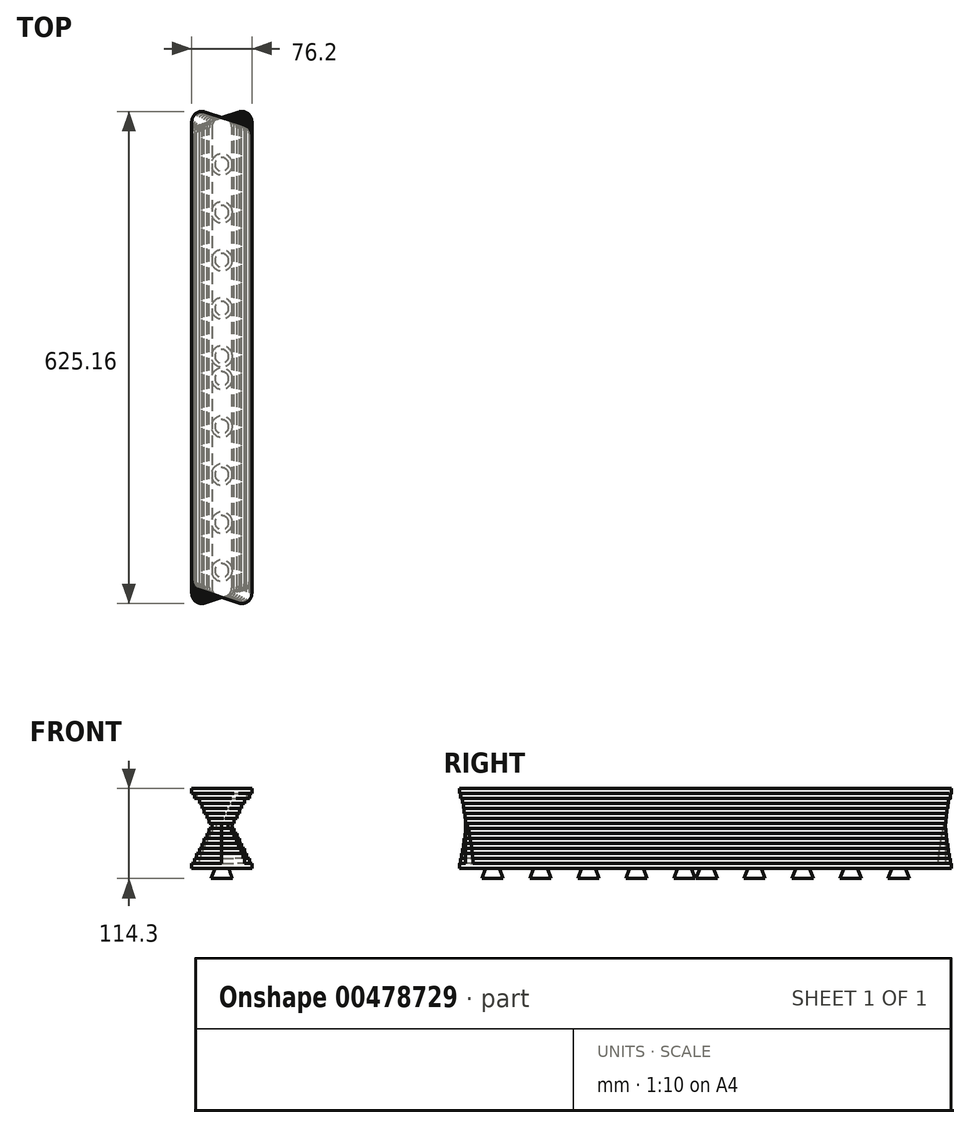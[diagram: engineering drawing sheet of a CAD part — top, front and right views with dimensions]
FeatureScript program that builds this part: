
annotation { "Feature Type Name" : "Feature", "Feature Type Description" : "" }
export const myFeature = defineFeature(function(context is Context, id is Id, definition is map)
    precondition{}
    {
        {
            var Q0;
            Q0=qCreatedBy(makeId("Top.planeOp"),FACE);
            var sketch = newSketch(context, id + "F0", { "sketchPlane" : qUnion([Q0])});
            skPoint(sketch, "E0", {"position": v(0, 0) * mm});
            skPoint(sketch, "E1", {"position": v(-38.1, 0) * mm});
            skPoint(sketch, "E2", {"position": v(-38.1, -304.8) * mm});
            skPoint(sketch, "E3", {"position": v(38.1, 0) * mm});
            skPoint(sketch, "E4", {"position": v(38.1, -279.4) * mm});
            skLineSegment(sketch, "E5", {"start": v(-38.1, 0) * mm, "end": v(-38.1, -287.18) * mm});
            skLineSegment(sketch, "E6", {"start": v(-21.38, -299.23) * mm, "end": v(29.42, -282.3) * mm});
            skLineSegment(sketch, "E7", {"start": v(38.1, -270.25) * mm, "end": v(38.1, 0) * mm});
            skArc(sketch, "E8.filletArc", {"start": v(-38.1, -287.18) * mm, "mid": v(-32.83, -297.48) * mm, "end": v(-21.38, -299.23) * mm});
            skArc(sketch, "E9.filletArc", {"start": v(29.42, -282.3) * mm, "mid": v(35.7, -277.67) * mm, "end": v(38.1, -270.25) * mm});
            skPoint(sketch, "E10", {"position": v(-38.1, 304.8) * mm});
            skPoint(sketch, "E11", {"position": v(38.1, 330.2) * mm});
            skLineSegment(sketch, "E12", {"start": v(-38.1, 0) * mm, "end": v(-38.1, 295.65) * mm});
            skLineSegment(sketch, "E13", {"start": v(-29.42, 307.7) * mm, "end": v(21.38, 324.63) * mm});
            skLineSegment(sketch, "E14", {"start": v(38.1, 312.58) * mm, "end": v(38.1, 0) * mm});
            skArc(sketch, "E15.filletArc", {"start": v(-29.42, 307.7) * mm, "mid": v(-35.7, 303.07) * mm, "end": v(-38.1, 295.65) * mm});
            skArc(sketch, "E16.filletArc", {"start": v(38.1, 312.58) * mm, "mid": v(32.83, 322.88) * mm, "end": v(21.38, 324.63) * mm});
            skSolve(sketch);
        }
        {
            var Q0;
            Q0=makeQuery(id+"F0.imprint","IMPRINT",FACE,{"disambiguationData":[TD([[makeQuery(id+"F0.imprint","IMPRINT",EDGE,{"derivedFrom":sQuery(id+"F0.wireOp",EDGE,"E5")}),1.0]])]});
            extrude(context, id + "F1", {"entities" : qUnion([Q0]), "depth" : 6.35 * mm});
        }
        {
            var Q0;
            Q0=makeQuery(id+"F1.opExtrude","CAP_FACE",FACE,{"disambiguationData":[OSD([sQuery(id+"F0.wireOp",EDGE,"E5"),sQuery(id+"F0.wireOp",EDGE,"E6"),sQuery(id+"F0.wireOp",EDGE,"E7"),sQuery(id+"F0.wireOp",EDGE,"E8.filletArc"),sQuery(id+"F0.wireOp",EDGE,"E9.filletArc"),sQuery(id+"F0.wireOp",EDGE,"E12"),sQuery(id+"F0.wireOp",EDGE,"E13"),sQuery(id+"F0.wireOp",EDGE,"E14"),sQuery(id+"F0.wireOp",EDGE,"E15.filletArc"),sQuery(id+"F0.wireOp",EDGE,"E16.filletArc")])],"isStart":false});
            var sketch = newSketch(context, id + "F2", { "sketchPlane" : qUnion([Q0])});
            skPoint(sketch, "E17", {"position": v(0, 0) * mm});
            skPoint(sketch, "E18", {"position": v(-34.93, 0) * mm});
            skPoint(sketch, "E19", {"position": v(-34.92, -303.21) * mm});
            skPoint(sketch, "E20", {"position": v(34.93, 0) * mm});
            skPoint(sketch, "E21", {"position": v(34.93, -280.99) * mm});
            skLineSegment(sketch, "E22", {"start": v(-34.93, 0) * mm, "end": v(-34.92, -285.84) * mm});
            skLineSegment(sketch, "E23", {"start": v(-18.37, -297.95) * mm, "end": v(26.08, -283.8) * mm});
            skLineSegment(sketch, "E24", {"start": v(34.93, -271.7) * mm, "end": v(34.93, 0) * mm});
            skArc(sketch, "E25.filletArc", {"start": v(-34.92, -285.84) * mm, "mid": v(-29.72, -296.1) * mm, "end": v(-18.37, -297.95) * mm});
            skArc(sketch, "E26.filletArc", {"start": v(26.08, -283.8) * mm, "mid": v(32.48, -279.2) * mm, "end": v(34.92, -271.7) * mm});
            skPoint(sketch, "E27", {"position": v(-34.93, 306.39) * mm});
            skPoint(sketch, "E28", {"position": v(34.92, 328.61) * mm});
            skLineSegment(sketch, "E29", {"start": v(-34.93, 0) * mm, "end": v(-34.93, 297.1) * mm});
            skLineSegment(sketch, "E30", {"start": v(-26.08, 309.2) * mm, "end": v(18.37, 323.35) * mm});
            skLineSegment(sketch, "E31", {"start": v(34.92, 311.24) * mm, "end": v(34.93, 0) * mm});
            skArc(sketch, "E32.filletArc", {"start": v(-26.08, 309.2) * mm, "mid": v(-32.48, 304.6) * mm, "end": v(-34.93, 297.1) * mm});
            skArc(sketch, "E33.filletArc", {"start": v(34.92, 311.24) * mm, "mid": v(29.72, 321.5) * mm, "end": v(18.37, 323.35) * mm});
            skSolve(sketch);
        }
        {
            var Q0;
            {var subQ8=sQuery(id+"F2.wireOp",EDGE,"E22");Q0=makeQuery(id+"F2.imprint","IMPRINT",FACE,{"disambiguationData":[TD([[makeQuery(id+"F2.imprint","IMPRINT",EDGE,{"derivedFrom":subQ8}),1.0]])]});}
            extrude(context, id + "F3", {"entities" : qUnion([Q0]), "depth" : 6.35 * mm});
        }
        {
            var Q0;
            Q0=makeQuery(id+"F3.opExtrude","CAP_FACE",FACE,{"disambiguationData":[OSD([sQuery(id+"F0.wireOp",EDGE,"E6"),sQuery(id+"F0.wireOp",EDGE,"E13"),sQuery(id+"F2.wireOp",EDGE,"E22"),sQuery(id+"F2.wireOp",EDGE,"E23"),sQuery(id+"F2.wireOp",EDGE,"E24"),sQuery(id+"F2.wireOp",EDGE,"E25.filletArc"),sQuery(id+"F2.wireOp",EDGE,"E26.filletArc"),sQuery(id+"F2.wireOp",EDGE,"E29"),sQuery(id+"F2.wireOp",EDGE,"E30"),sQuery(id+"F2.wireOp",EDGE,"E31"),sQuery(id+"F2.wireOp",EDGE,"E32.filletArc"),sQuery(id+"F2.wireOp",EDGE,"E33.filletArc")])],"isStart":false});
            var sketch = newSketch(context, id + "F4", { "sketchPlane" : qUnion([Q0])});
            skPoint(sketch, "E34", {"position": v(0, 0) * mm});
            skPoint(sketch, "E35", {"position": v(-31.75, 0) * mm});
            skPoint(sketch, "E36", {"position": v(-31.75, -301.63) * mm});
            skPoint(sketch, "E37", {"position": v(31.75, 0) * mm});
            skPoint(sketch, "E38", {"position": v(31.75, -282.58) * mm});
            skLineSegment(sketch, "E39", {"start": v(-31.75, 0) * mm, "end": v(-31.75, -284.56) * mm});
            skLineSegment(sketch, "E40", {"start": v(-15.4, -296.72) * mm, "end": v(22.7, -285.3) * mm});
            skLineSegment(sketch, "E41", {"start": v(31.75, -273.13) * mm, "end": v(31.75, 0) * mm});
            skArc(sketch, "E42.filletArc", {"start": v(-31.75, -284.56) * mm, "mid": v(-26.63, -294.74) * mm, "end": v(-15.4, -296.72) * mm});
            skArc(sketch, "E43.filletArc", {"start": v(22.7, -285.3) * mm, "mid": v(29.24, -280.7) * mm, "end": v(31.75, -273.13) * mm});
            skPoint(sketch, "E44.MirrorP", {"position": v(-461.86, 195.96) * mm});
            skPoint(sketch, "E45", {"position": v(-31.75, 307.98) * mm});
            skPoint(sketch, "E46", {"position": v(31.75, 327.03) * mm});
            skLineSegment(sketch, "E47", {"start": v(-31.75, 0) * mm, "end": v(-31.75, 298.53) * mm});
            skLineSegment(sketch, "E48", {"start": v(-22.7, 310.7) * mm, "end": v(15.4, 322.12) * mm});
            skLineSegment(sketch, "E49", {"start": v(31.75, 309.96) * mm, "end": v(31.75, 0) * mm});
            skArc(sketch, "E50.filletArc", {"start": v(-22.7, 310.7) * mm, "mid": v(-29.24, 306.1) * mm, "end": v(-31.75, 298.53) * mm});
            skArc(sketch, "E51.filletArc", {"start": v(31.75, 309.96) * mm, "mid": v(26.63, 320.14) * mm, "end": v(15.4, 322.12) * mm});
            skSolve(sketch);
        }
        {
            var Q0;
            {var subQ8=sQuery(id+"F4.wireOp",EDGE,"E39");Q0=makeQuery(id+"F4.imprint","IMPRINT",FACE,{"disambiguationData":[TD([[makeQuery(id+"F4.imprint","IMPRINT",EDGE,{"derivedFrom":subQ8}),1.0]])]});}
            extrude(context, id + "F5", {"entities" : qUnion([Q0]), "depth" : 6.35 * mm});
        }
        {
            var Q0;
            Q0=makeQuery(id+"F5.opExtrude","CAP_FACE",FACE,{"disambiguationData":[OSD([sQuery(id+"F0.wireOp",EDGE,"E6"),sQuery(id+"F0.wireOp",EDGE,"E13"),sQuery(id+"F4.wireOp",EDGE,"E39"),sQuery(id+"F4.wireOp",EDGE,"E40"),sQuery(id+"F4.wireOp",EDGE,"E41"),sQuery(id+"F4.wireOp",EDGE,"E42.filletArc"),sQuery(id+"F4.wireOp",EDGE,"E43.filletArc"),sQuery(id+"F4.wireOp",EDGE,"E47"),sQuery(id+"F4.wireOp",EDGE,"E48"),sQuery(id+"F4.wireOp",EDGE,"E49"),sQuery(id+"F4.wireOp",EDGE,"E50.filletArc"),sQuery(id+"F4.wireOp",EDGE,"E51.filletArc")])],"isStart":false});
            var sketch = newSketch(context, id + "F6", { "sketchPlane" : qUnion([Q0])});
            skPoint(sketch, "E52", {"position": v(0, 0) * mm});
            skPoint(sketch, "E53", {"position": v(-28.58, 0) * mm});
            skPoint(sketch, "E54", {"position": v(-28.57, -300.04) * mm});
            skPoint(sketch, "E55", {"position": v(28.58, 0) * mm});
            skPoint(sketch, "E56", {"position": v(28.58, -284.16) * mm});
            skLineSegment(sketch, "E57", {"start": v(-28.58, 0) * mm, "end": v(-28.57, -283.33) * mm});
            skLineSegment(sketch, "E58", {"start": v(-12.48, -295.57) * mm, "end": v(19.27, -286.75) * mm});
            skLineSegment(sketch, "E59", {"start": v(28.58, -274.5) * mm, "end": v(28.58, 0) * mm});
            skArc(sketch, "E60.filletArc", {"start": v(-28.57, -283.33) * mm, "mid": v(-23.56, -293.44) * mm, "end": v(-12.48, -295.57) * mm});
            skArc(sketch, "E61.filletArc", {"start": v(19.27, -286.75) * mm, "mid": v(25.99, -282.2) * mm, "end": v(28.57, -274.5) * mm});
            skPoint(sketch, "E62.MirrorP", {"position": v(-895.77, 331.85) * mm});
            skPoint(sketch, "E63", {"position": v(-28.58, 309.56) * mm});
            skPoint(sketch, "E64", {"position": v(28.57, 325.44) * mm});
            skLineSegment(sketch, "E65", {"start": v(-28.58, 0) * mm, "end": v(-28.58, 299.9) * mm});
            skLineSegment(sketch, "E66", {"start": v(-19.27, 312.15) * mm, "end": v(12.48, 320.97) * mm});
            skLineSegment(sketch, "E67", {"start": v(28.57, 308.73) * mm, "end": v(28.58, 0) * mm});
            skArc(sketch, "E68.filletArc", {"start": v(-19.27, 312.15) * mm, "mid": v(-25.99, 307.6) * mm, "end": v(-28.58, 299.9) * mm});
            skArc(sketch, "E69.filletArc", {"start": v(28.57, 308.73) * mm, "mid": v(23.56, 318.84) * mm, "end": v(12.48, 320.97) * mm});
            skSolve(sketch);
        }
        {
            var Q0;
            Q0=makeQuery(id+"F6.imprint","IMPRINT",FACE,{"disambiguationData":[TD([[makeQuery(id+"F6.imprint","IMPRINT",EDGE,{"derivedFrom":sQuery(id+"F6.wireOp",EDGE,"E57")}),1.0]])]});
            extrude(context, id + "F7", {"entities" : qUnion([Q0]), "depth" : 6.35 * mm});
        }
        {
            var Q0;
            Q0=makeQuery(id+"F7.opExtrude","CAP_FACE",FACE,{"disambiguationData":[OSD([sQuery(id+"F0.wireOp",EDGE,"E6"),sQuery(id+"F0.wireOp",EDGE,"E13"),sQuery(id+"F6.wireOp",EDGE,"E57"),sQuery(id+"F6.wireOp",EDGE,"E58"),sQuery(id+"F6.wireOp",EDGE,"E59"),sQuery(id+"F6.wireOp",EDGE,"E60.filletArc"),sQuery(id+"F6.wireOp",EDGE,"E61.filletArc"),sQuery(id+"F6.wireOp",EDGE,"E65"),sQuery(id+"F6.wireOp",EDGE,"E66"),sQuery(id+"F6.wireOp",EDGE,"E67"),sQuery(id+"F6.wireOp",EDGE,"E68.filletArc"),sQuery(id+"F6.wireOp",EDGE,"E69.filletArc")])],"isStart":false});
            var sketch = newSketch(context, id + "F8", { "sketchPlane" : qUnion([Q0])});
            skPoint(sketch, "E70", {"position": v(0, 0) * mm});
            skPoint(sketch, "E71", {"position": v(-25.4, 0) * mm});
            skPoint(sketch, "E72", {"position": v(-25.4, -298.45) * mm});
            skPoint(sketch, "E73", {"position": v(25.4, 0) * mm});
            skPoint(sketch, "E74", {"position": v(25.4, -285.75) * mm});
            skLineSegment(sketch, "E75", {"start": v(-25.4, 0) * mm, "end": v(-25.4, -282.18) * mm});
            skLineSegment(sketch, "E76", {"start": v(-9.62, -294.5) * mm, "end": v(15.78, -288.15) * mm});
            skLineSegment(sketch, "E77", {"start": v(25.4, -275.83) * mm, "end": v(25.4, 0) * mm});
            skArc(sketch, "E78.filletArc", {"start": v(-25.4, -282.18) * mm, "mid": v(-20.52, -292.2) * mm, "end": v(-9.62, -294.5) * mm});
            skArc(sketch, "E79.filletArc", {"start": v(15.78, -288.15) * mm, "mid": v(22.71, -283.65) * mm, "end": v(25.4, -275.83) * mm});
            skPoint(sketch, "E80.MirrorP", {"position": v(-1189.04, 488.26) * mm});
            skPoint(sketch, "E81", {"position": v(-25.4, 311.15) * mm});
            skPoint(sketch, "E82", {"position": v(25.4, 323.85) * mm});
            skLineSegment(sketch, "E83", {"start": v(-25.4, 0) * mm, "end": v(-25.4, 301.23) * mm});
            skLineSegment(sketch, "E84", {"start": v(-15.78, 313.55) * mm, "end": v(9.62, 319.9) * mm});
            skLineSegment(sketch, "E85", {"start": v(25.4, 307.58) * mm, "end": v(25.4, 0) * mm});
            skArc(sketch, "E86.filletArc", {"start": v(-15.78, 313.55) * mm, "mid": v(-22.71, 309.05) * mm, "end": v(-25.4, 301.23) * mm});
            skArc(sketch, "E87.filletArc", {"start": v(25.4, 307.58) * mm, "mid": v(20.52, 317.6) * mm, "end": v(9.62, 319.9) * mm});
            skSolve(sketch);
        }
        {
            var Q0;
            Q0=makeQuery(id+"F8.imprint","IMPRINT",FACE,{"disambiguationData":[TD([[makeQuery(id+"F8.imprint","IMPRINT",EDGE,{"derivedFrom":sQuery(id+"F8.wireOp",EDGE,"E75")}),1.0]])]});
            extrude(context, id + "F9", {"entities" : qUnion([Q0]), "depth" : 6.35 * mm});
        }
        {
            var Q0;
            Q0=makeQuery(id+"F9.opExtrude","CAP_FACE",FACE,{"disambiguationData":[OSD([sQuery(id+"F0.wireOp",EDGE,"E6"),sQuery(id+"F0.wireOp",EDGE,"E13"),sQuery(id+"F8.wireOp",EDGE,"E75"),sQuery(id+"F8.wireOp",EDGE,"E76"),sQuery(id+"F8.wireOp",EDGE,"E77"),sQuery(id+"F8.wireOp",EDGE,"E78.filletArc"),sQuery(id+"F8.wireOp",EDGE,"E79.filletArc"),sQuery(id+"F8.wireOp",EDGE,"E83"),sQuery(id+"F8.wireOp",EDGE,"E84"),sQuery(id+"F8.wireOp",EDGE,"E85"),sQuery(id+"F8.wireOp",EDGE,"E86.filletArc"),sQuery(id+"F8.wireOp",EDGE,"E87.filletArc")])],"isStart":false});
            var sketch = newSketch(context, id + "F10", { "sketchPlane" : qUnion([Q0])});
            skPoint(sketch, "E88", {"position": v(0, 0) * mm});
            skPoint(sketch, "E89", {"position": v(-22.23, 0) * mm});
            skPoint(sketch, "E90", {"position": v(-22.22, -296.86) * mm});
            skPoint(sketch, "E91", {"position": v(22.23, 0) * mm});
            skPoint(sketch, "E92", {"position": v(22.23, -287.34) * mm});
            skLineSegment(sketch, "E93", {"start": v(-22.23, 0) * mm, "end": v(-22.22, -281.15) * mm});
            skLineSegment(sketch, "E94", {"start": v(-6.86, -293.57) * mm, "end": v(12.19, -289.49) * mm});
            skLineSegment(sketch, "E95", {"start": v(22.23, -277.07) * mm, "end": v(22.23, 0) * mm});
            skArc(sketch, "E96.filletArc", {"start": v(-22.22, -281.15) * mm, "mid": v(-17.5, -291.03) * mm, "end": v(-6.86, -293.57) * mm});
            skArc(sketch, "E97.filletArc", {"start": v(12.19, -289.49) * mm, "mid": v(19.4, -285.05) * mm, "end": v(22.22, -277.07) * mm});
            skPoint(sketch, "E98.MirrorP", {"position": v(-1110.6, 407.11) * mm});
            skPoint(sketch, "E99", {"position": v(-22.23, 312.74) * mm});
            skPoint(sketch, "E100", {"position": v(22.22, 322.26) * mm});
            skLineSegment(sketch, "E101", {"start": v(-22.23, 0) * mm, "end": v(-22.23, 302.47) * mm});
            skLineSegment(sketch, "E102", {"start": v(-12.19, 314.89) * mm, "end": v(6.86, 318.97) * mm});
            skLineSegment(sketch, "E103", {"start": v(22.22, 306.55) * mm, "end": v(22.23, 0) * mm});
            skArc(sketch, "E104.filletArc", {"start": v(-12.19, 314.89) * mm, "mid": v(-19.4, 310.45) * mm, "end": v(-22.23, 302.47) * mm});
            skArc(sketch, "E105.filletArc", {"start": v(22.22, 306.55) * mm, "mid": v(17.5, 316.43) * mm, "end": v(6.86, 318.97) * mm});
            skSolve(sketch);
        }
        {
            var Q0;
            Q0=makeQuery(id+"F10.imprint","IMPRINT",FACE,{"disambiguationData":[TD([[makeQuery(id+"F10.imprint","IMPRINT",EDGE,{"derivedFrom":sQuery(id+"F10.wireOp",EDGE,"E93")}),1.0]])]});
            extrude(context, id + "F11", {"entities" : qUnion([Q0]), "depth" : 6.35 * mm});
        }
        {
            var Q0;
            Q0=makeQuery(id+"F11.opExtrude","CAP_FACE",FACE,{"disambiguationData":[OSD([sQuery(id+"F0.wireOp",EDGE,"E6"),sQuery(id+"F0.wireOp",EDGE,"E13"),sQuery(id+"F10.wireOp",EDGE,"E93"),sQuery(id+"F10.wireOp",EDGE,"E94"),sQuery(id+"F10.wireOp",EDGE,"E95"),sQuery(id+"F10.wireOp",EDGE,"E96.filletArc"),sQuery(id+"F10.wireOp",EDGE,"E97.filletArc"),sQuery(id+"F10.wireOp",EDGE,"E101"),sQuery(id+"F10.wireOp",EDGE,"E102"),sQuery(id+"F10.wireOp",EDGE,"E103"),sQuery(id+"F10.wireOp",EDGE,"E104.filletArc"),sQuery(id+"F10.wireOp",EDGE,"E105.filletArc")])],"isStart":false});
            var sketch = newSketch(context, id + "F12", { "sketchPlane" : qUnion([Q0])});
            skPoint(sketch, "E106", {"position": v(0, 0) * mm});
            skPoint(sketch, "E107", {"position": v(-19.05, 0) * mm});
            skPoint(sketch, "E108", {"position": v(-19.05, -295.28) * mm});
            skPoint(sketch, "E109", {"position": v(19.05, 0) * mm});
            skPoint(sketch, "E110", {"position": v(19.05, -288.93) * mm});
            skLineSegment(sketch, "E111", {"start": v(-19.05, 0) * mm, "end": v(-19.05, -280.28) * mm});
            skLineSegment(sketch, "E112", {"start": v(-4.26, -292.81) * mm, "end": v(8.44, -290.7) * mm});
            skLineSegment(sketch, "E113", {"start": v(19.05, -278.17) * mm, "end": v(19.05, 0) * mm});
            skArc(sketch, "E114.filletArc", {"start": v(-19.05, -280.28) * mm, "mid": v(-14.56, -289.97) * mm, "end": v(-4.26, -292.81) * mm});
            skArc(sketch, "E115.filletArc", {"start": v(8.44, -290.7) * mm, "mid": v(16.04, -286.38) * mm, "end": v(19.05, -278.17) * mm});
            skPoint(sketch, "E116.MirrorP", {"position": v(-1134.4, 517.38) * mm});
            skPoint(sketch, "E117", {"position": v(-19.05, 314.33) * mm});
            skPoint(sketch, "E118", {"position": v(19.05, 320.68) * mm});
            skLineSegment(sketch, "E119", {"start": v(-19.05, 0) * mm, "end": v(-19.05, 303.57) * mm});
            skLineSegment(sketch, "E120", {"start": v(-8.44, 316.1) * mm, "end": v(4.26, 318.21) * mm});
            skLineSegment(sketch, "E121", {"start": v(19.05, 305.68) * mm, "end": v(19.05, 0) * mm});
            skArc(sketch, "E122.filletArc", {"start": v(-8.44, 316.1) * mm, "mid": v(-16.04, 311.78) * mm, "end": v(-19.05, 303.57) * mm});
            skArc(sketch, "E123.filletArc", {"start": v(19.05, 305.68) * mm, "mid": v(14.56, 315.37) * mm, "end": v(4.26, 318.21) * mm});
            skSolve(sketch);
        }
        {
            var Q0;
            {var subQ12=sQuery(id+"F12.wireOp",EDGE,"E113");Q0=makeQuery(id+"F12.imprint","IMPRINT",FACE,{"disambiguationData":[TD([[makeQuery(id+"F12.imprint","IMPRINT",EDGE,{"derivedFrom":subQ12}),1.0]])]});}
            extrude(context, id + "F13", {"entities" : qUnion([Q0]), "depth" : 6.35 * mm});
        }
        {
            var Q0;
            Q0=makeQuery(id+"F13.opExtrude","CAP_FACE",FACE,{"disambiguationData":[OSD([sQuery(id+"F0.wireOp",EDGE,"E6"),sQuery(id+"F0.wireOp",EDGE,"E13"),sQuery(id+"F10.wireOp",EDGE,"E93"),sQuery(id+"F10.wireOp",EDGE,"E96.filletArc"),sQuery(id+"F10.wireOp",EDGE,"E101"),sQuery(id+"F10.wireOp",EDGE,"E102"),sQuery(id+"F10.wireOp",EDGE,"E104.filletArc"),sQuery(id+"F12.wireOp",EDGE,"E112"),sQuery(id+"F12.wireOp",EDGE,"E113"),sQuery(id+"F12.wireOp",EDGE,"E115.filletArc"),sQuery(id+"F12.wireOp",EDGE,"E121"),sQuery(id+"F12.wireOp",EDGE,"E123.filletArc")])],"isStart":false});
            var sketch = newSketch(context, id + "F14", { "sketchPlane" : qUnion([Q0])});
            skPoint(sketch, "E124", {"position": v(0, 0) * mm});
            skPoint(sketch, "E125", {"position": v(-15.88, 0) * mm});
            skPoint(sketch, "E126", {"position": v(-15.87, -293.69) * mm});
            skPoint(sketch, "E127", {"position": v(15.88, 0) * mm});
            skPoint(sketch, "E128", {"position": v(15.88, -290.51) * mm});
            skLineSegment(sketch, "E129", {"start": v(-15.88, 0) * mm, "end": v(-15.87, -279.65) * mm});
            skLineSegment(sketch, "E130", {"start": v(-1.91, -292.3) * mm, "end": v(4.44, -291.66) * mm});
            skLineSegment(sketch, "E131", {"start": v(15.88, -279.02) * mm, "end": v(15.88, 0) * mm});
            skArc(sketch, "E132.filletArc", {"start": v(-15.87, -279.65) * mm, "mid": v(-11.7, -289.07) * mm, "end": v(-1.91, -292.3) * mm});
            skArc(sketch, "E133.filletArc", {"start": v(4.44, -291.66) * mm, "mid": v(12.6, -287.54) * mm, "end": v(15.88, -279.02) * mm});
            skPoint(sketch, "E134.MirrorP", {"position": v(-1354.1, 474.43) * mm});
            skPoint(sketch, "E135", {"position": v(-15.88, 315.91) * mm});
            skPoint(sketch, "E136", {"position": v(15.87, 319.09) * mm});
            skLineSegment(sketch, "E137", {"start": v(-15.88, 0) * mm, "end": v(-15.88, 304.42) * mm});
            skLineSegment(sketch, "E138", {"start": v(-4.44, 317.06) * mm, "end": v(1.91, 317.7) * mm});
            skLineSegment(sketch, "E139", {"start": v(15.87, 305.05) * mm, "end": v(15.88, 0) * mm});
            skArc(sketch, "E140.filletArc", {"start": v(-4.44, 317.06) * mm, "mid": v(-12.6, 312.94) * mm, "end": v(-15.88, 304.42) * mm});
            skArc(sketch, "E141.filletArc", {"start": v(15.87, 305.05) * mm, "mid": v(11.7, 314.47) * mm, "end": v(1.91, 317.7) * mm});
            skSolve(sketch);
        }
        {
            var Q0;
            Q0=makeQuery(id+"F14.imprint","IMPRINT",FACE,{"disambiguationData":[TD([[makeQuery(id+"F14.imprint","IMPRINT",EDGE,{"derivedFrom":sQuery(id+"F14.wireOp",EDGE,"E129")}),1.0]])]});
            extrude(context, id + "F15", {"entities" : qUnion([Q0]), "depth" : 6.35 * mm});
        }
        {
            var Q0;
            Q0=makeQuery(id+"F15.opExtrude","CAP_FACE",FACE,{"disambiguationData":[OSD([sQuery(id+"F0.wireOp",EDGE,"E6"),sQuery(id+"F0.wireOp",EDGE,"E13"),sQuery(id+"F14.wireOp",EDGE,"E129"),sQuery(id+"F14.wireOp",EDGE,"E130"),sQuery(id+"F14.wireOp",EDGE,"E131"),sQuery(id+"F14.wireOp",EDGE,"E132.filletArc"),sQuery(id+"F14.wireOp",EDGE,"E133.filletArc"),sQuery(id+"F14.wireOp",EDGE,"E137"),sQuery(id+"F14.wireOp",EDGE,"E138"),sQuery(id+"F14.wireOp",EDGE,"E139"),sQuery(id+"F14.wireOp",EDGE,"E140.filletArc"),sQuery(id+"F14.wireOp",EDGE,"E141.filletArc")])],"isStart":false});
            var sketch = newSketch(context, id + "F16", { "sketchPlane" : qUnion([Q0])});
            skPoint(sketch, "E142", {"position": v(0, 0) * mm});
            skPoint(sketch, "E143", {"position": v(-12.7, 0) * mm});
            skPoint(sketch, "E144", {"position": v(-12.7, -292.1) * mm});
            skPoint(sketch, "E145", {"position": v(12.7, 0) * mm});
            skPoint(sketch, "E146", {"position": v(12.7, -292.1) * mm});
            skLineSegment(sketch, "E147", {"start": v(-12.7, 0) * mm, "end": v(-12.7, -279.4) * mm});
            skLineSegment(sketch, "E148", {"start": v(0, -292.1) * mm, "end": v(0, -292.1) * mm});
            skLineSegment(sketch, "E149", {"start": v(12.7, -279.4) * mm, "end": v(12.7, 0) * mm});
            skArc(sketch, "E150.filletArc", {"start": v(-12.7, -279.4) * mm, "mid": v(-8.98, -288.38) * mm, "end": v(0, -292.1) * mm});
            skArc(sketch, "E151.filletArc", {"start": v(0, -292.1) * mm, "mid": v(8.98, -288.38) * mm, "end": v(12.7, -279.4) * mm});
            skPoint(sketch, "E152.MirrorP", {"position": v(-1174.77, 259.43) * mm});
            skPoint(sketch, "E153", {"position": v(-12.7, 317.5) * mm});
            skPoint(sketch, "E154", {"position": v(12.7, 317.5) * mm});
            skLineSegment(sketch, "E155", {"start": v(-12.7, 0) * mm, "end": v(-12.7, 304.8) * mm});
            skLineSegment(sketch, "E156", {"start": v(0, 317.5) * mm, "end": v(0, 317.5) * mm});
            skLineSegment(sketch, "E157", {"start": v(12.7, 304.8) * mm, "end": v(12.7, 0) * mm});
            skArc(sketch, "E158.filletArc", {"start": v(0, 317.5) * mm, "mid": v(-8.98, 313.78) * mm, "end": v(-12.7, 304.8) * mm});
            skArc(sketch, "E159.filletArc", {"start": v(12.7, 304.8) * mm, "mid": v(8.98, 313.78) * mm, "end": v(0, 317.5) * mm});
            skSolve(sketch);
        }
        {
            var Q0;
            Q0=makeQuery(id+"F16.imprint","IMPRINT",FACE,{"disambiguationData":[TD([[makeQuery(id+"F16.imprint","IMPRINT",EDGE,{"derivedFrom":sQuery(id+"F16.wireOp",EDGE,"E147")}),1.0]])]});
            extrude(context, id + "F17", {"entities" : qUnion([Q0]), "depth" : 6.35 * mm});
        }
        {
            var Q0;
            Q0=makeQuery(id+"F17.opExtrude","CAP_FACE",FACE,{"disambiguationData":[OSD([sQuery(id+"F0.wireOp",EDGE,"E6"),sQuery(id+"F0.wireOp",EDGE,"E13"),sQuery(id+"F16.wireOp",EDGE,"E147"),sQuery(id+"F16.wireOp",EDGE,"E149"),sQuery(id+"F16.wireOp",EDGE,"E150.filletArc"),sQuery(id+"F16.wireOp",EDGE,"E151.filletArc"),sQuery(id+"F16.wireOp",EDGE,"E155"),sQuery(id+"F16.wireOp",EDGE,"E157"),sQuery(id+"F16.wireOp",EDGE,"E158.filletArc"),sQuery(id+"F16.wireOp",EDGE,"E159.filletArc")])],"isStart":false});
            var sketch = newSketch(context, id + "F18", { "sketchPlane" : qUnion([Q0])});
            skPoint(sketch, "E160", {"position": v(0, 0) * mm});
            skPoint(sketch, "E161", {"position": v(-15.88, 0) * mm});
            skPoint(sketch, "E162", {"position": v(-15.87, -290.51) * mm});
            skPoint(sketch, "E163", {"position": v(15.88, 0) * mm});
            skPoint(sketch, "E164", {"position": v(15.88, -293.69) * mm});
            skLineSegment(sketch, "E165", {"start": v(-15.88, 0) * mm, "end": v(-15.87, -279.02) * mm});
            skLineSegment(sketch, "E166", {"start": v(-4.44, -291.66) * mm, "end": v(1.91, -292.3) * mm});
            skLineSegment(sketch, "E167", {"start": v(15.88, -279.65) * mm, "end": v(15.88, 0) * mm});
            skArc(sketch, "E168.filletArc", {"start": v(-15.87, -279.02) * mm, "mid": v(-12.6, -287.54) * mm, "end": v(-4.44, -291.66) * mm});
            skArc(sketch, "E169.filletArc", {"start": v(1.91, -292.3) * mm, "mid": v(11.7, -289.07) * mm, "end": v(15.87, -279.65) * mm});
            skPoint(sketch, "E170.MirrorP", {"position": v(-1386.88, 490.35) * mm});
            skPoint(sketch, "E171", {"position": v(-15.88, 319.09) * mm});
            skPoint(sketch, "E172", {"position": v(15.87, 315.91) * mm});
            skLineSegment(sketch, "E173", {"start": v(-15.88, 0) * mm, "end": v(-15.88, 305.05) * mm});
            skLineSegment(sketch, "E174", {"start": v(-1.91, 317.7) * mm, "end": v(4.44, 317.06) * mm});
            skLineSegment(sketch, "E175", {"start": v(15.87, 304.42) * mm, "end": v(15.88, 0) * mm});
            skArc(sketch, "E176.filletArc", {"start": v(-1.91, 317.7) * mm, "mid": v(-11.7, 314.47) * mm, "end": v(-15.88, 305.05) * mm});
            skArc(sketch, "E177.filletArc", {"start": v(15.87, 304.42) * mm, "mid": v(12.6, 312.94) * mm, "end": v(4.44, 317.06) * mm});
            skSolve(sketch);
        }
        {
            var Q0;
            Q0=qSketchRegion(id+"F18",true);
            extrude(context, id + "F19", {"entities" : qUnion([Q0]), "depth" : 6.35 * mm});
        }
        {
            var Q0;
            Q0=makeQuery(id+"F19.opExtrude","CAP_FACE",FACE,{"disambiguationData":[OSD([sQuery(id+"F0.wireOp",EDGE,"E6"),sQuery(id+"F0.wireOp",EDGE,"E13"),sQuery(id+"F16.wireOp",EDGE,"E147"),sQuery(id+"F16.wireOp",EDGE,"E149"),sQuery(id+"F16.wireOp",EDGE,"E150.filletArc"),sQuery(id+"F16.wireOp",EDGE,"E151.filletArc"),sQuery(id+"F16.wireOp",EDGE,"E155"),sQuery(id+"F16.wireOp",EDGE,"E157"),sQuery(id+"F16.wireOp",EDGE,"E158.filletArc"),sQuery(id+"F16.wireOp",EDGE,"E159.filletArc"),sQuery(id+"F18.wireOp",EDGE,"E166"),sQuery(id+"F18.wireOp",EDGE,"E174")])],"isStart":false});
            var sketch = newSketch(context, id + "F20", { "sketchPlane" : qUnion([Q0])});
            skPoint(sketch, "E178", {"position": v(0, 0) * mm});
            skPoint(sketch, "E179", {"position": v(-19.05, 0) * mm});
            skPoint(sketch, "E180", {"position": v(-19.05, -288.93) * mm});
            skPoint(sketch, "E181", {"position": v(19.05, 0) * mm});
            skPoint(sketch, "E182", {"position": v(19.05, -295.28) * mm});
            skLineSegment(sketch, "E183", {"start": v(-19.05, 0) * mm, "end": v(-19.05, -278.17) * mm});
            skLineSegment(sketch, "E184", {"start": v(-8.44, -290.7) * mm, "end": v(4.26, -292.81) * mm});
            skLineSegment(sketch, "E185", {"start": v(19.05, -280.28) * mm, "end": v(19.05, 0) * mm});
            skArc(sketch, "E186.filletArc", {"start": v(-19.05, -278.17) * mm, "mid": v(-16.04, -286.38) * mm, "end": v(-8.44, -290.7) * mm});
            skArc(sketch, "E187.filletArc", {"start": v(4.26, -292.81) * mm, "mid": v(14.56, -289.97) * mm, "end": v(19.05, -280.28) * mm});
            skPoint(sketch, "E188.MirrorP", {"position": v(-2251.33, 639) * mm});
            skPoint(sketch, "E189", {"position": v(-19.05, 320.68) * mm});
            skPoint(sketch, "E190", {"position": v(19.05, 314.33) * mm});
            skLineSegment(sketch, "E191", {"start": v(-19.05, 0) * mm, "end": v(-19.05, 305.68) * mm});
            skLineSegment(sketch, "E192", {"start": v(-4.26, 318.21) * mm, "end": v(8.44, 316.1) * mm});
            skLineSegment(sketch, "E193", {"start": v(19.05, 303.57) * mm, "end": v(19.05, 0) * mm});
            skArc(sketch, "E194.filletArc", {"start": v(-4.26, 318.21) * mm, "mid": v(-14.56, 315.37) * mm, "end": v(-19.05, 305.68) * mm});
            skArc(sketch, "E195.filletArc", {"start": v(19.05, 303.57) * mm, "mid": v(16.04, 311.78) * mm, "end": v(8.44, 316.1) * mm});
            skSolve(sketch);
        }
        {
            var Q0;
            Q0=qSketchRegion(id+"F20",true);
            extrude(context, id + "F21", {"entities" : qUnion([Q0]), "depth" : 6.35 * mm});
        }
        {
            var Q0;
            Q0=makeQuery(id+"F21.opExtrude","CAP_FACE",FACE,{"disambiguationData":[OSD([sQuery(id+"F0.wireOp",EDGE,"E6"),sQuery(id+"F0.wireOp",EDGE,"E13"),sQuery(id+"F16.wireOp",EDGE,"E147"),sQuery(id+"F16.wireOp",EDGE,"E149"),sQuery(id+"F16.wireOp",EDGE,"E150.filletArc"),sQuery(id+"F16.wireOp",EDGE,"E151.filletArc"),sQuery(id+"F16.wireOp",EDGE,"E155"),sQuery(id+"F16.wireOp",EDGE,"E157"),sQuery(id+"F16.wireOp",EDGE,"E158.filletArc"),sQuery(id+"F16.wireOp",EDGE,"E159.filletArc"),sQuery(id+"F20.wireOp",EDGE,"E184"),sQuery(id+"F20.wireOp",EDGE,"E192")])],"isStart":false});
            var sketch = newSketch(context, id + "F22", { "sketchPlane" : qUnion([Q0])});
            skPoint(sketch, "E196", {"position": v(0, 0) * mm});
            skPoint(sketch, "E197", {"position": v(-22.23, 0) * mm});
            skPoint(sketch, "E198", {"position": v(-22.22, -287.34) * mm});
            skPoint(sketch, "E199", {"position": v(22.23, 0) * mm});
            skPoint(sketch, "E200", {"position": v(22.23, -296.86) * mm});
            skLineSegment(sketch, "E201", {"start": v(-22.23, 0) * mm, "end": v(-22.22, -277.07) * mm});
            skLineSegment(sketch, "E202", {"start": v(-12.19, -289.49) * mm, "end": v(6.86, -293.57) * mm});
            skLineSegment(sketch, "E203", {"start": v(22.23, -281.15) * mm, "end": v(22.23, 0) * mm});
            skArc(sketch, "E204.filletArc", {"start": v(-22.22, -277.07) * mm, "mid": v(-19.4, -285.05) * mm, "end": v(-12.19, -289.49) * mm});
            skArc(sketch, "E205.filletArc", {"start": v(6.86, -293.57) * mm, "mid": v(17.5, -291.03) * mm, "end": v(22.22, -281.15) * mm});
            skPoint(sketch, "E206.MirrorP", {"position": v(-2054.65, 833.78) * mm});
            skPoint(sketch, "E207", {"position": v(-22.23, 322.26) * mm});
            skPoint(sketch, "E208", {"position": v(22.22, 312.74) * mm});
            skLineSegment(sketch, "E209", {"start": v(-22.23, 0) * mm, "end": v(-22.23, 306.55) * mm});
            skLineSegment(sketch, "E210", {"start": v(-6.86, 318.97) * mm, "end": v(12.19, 314.89) * mm});
            skLineSegment(sketch, "E211", {"start": v(22.22, 302.47) * mm, "end": v(22.23, 0) * mm});
            skArc(sketch, "E212.filletArc", {"start": v(-6.86, 318.97) * mm, "mid": v(-17.5, 316.43) * mm, "end": v(-22.23, 306.55) * mm});
            skArc(sketch, "E213.filletArc", {"start": v(22.22, 302.47) * mm, "mid": v(19.4, 310.45) * mm, "end": v(12.19, 314.89) * mm});
            skSolve(sketch);
        }
        {
            var Q0;
            Q0=qSketchRegion(id+"F22",true);
            extrude(context, id + "F23", {"entities" : qUnion([Q0]), "depth" : 6.35 * mm});
        }
        {
            var Q0;
            Q0=makeQuery(id+"F23.opExtrude","CAP_FACE",FACE,{"disambiguationData":[OSD([sQuery(id+"F22.wireOp",EDGE,"E201"),sQuery(id+"F22.wireOp",EDGE,"E202"),sQuery(id+"F22.wireOp",EDGE,"E203"),sQuery(id+"F22.wireOp",EDGE,"E204.filletArc"),sQuery(id+"F22.wireOp",EDGE,"E205.filletArc"),sQuery(id+"F22.wireOp",EDGE,"E209"),sQuery(id+"F22.wireOp",EDGE,"E210"),sQuery(id+"F22.wireOp",EDGE,"E211"),sQuery(id+"F22.wireOp",EDGE,"E212.filletArc"),sQuery(id+"F22.wireOp",EDGE,"E213.filletArc")])],"isStart":false});
            var sketch = newSketch(context, id + "F24", { "sketchPlane" : qUnion([Q0])});
            skPoint(sketch, "E214", {"position": v(0, 0) * mm});
            skPoint(sketch, "E215", {"position": v(-25.4, 0) * mm});
            skPoint(sketch, "E216", {"position": v(-25.4, -285.75) * mm});
            skPoint(sketch, "E217", {"position": v(25.4, 0) * mm});
            skPoint(sketch, "E218", {"position": v(25.4, -298.45) * mm});
            skLineSegment(sketch, "E219", {"start": v(-25.4, 0) * mm, "end": v(-25.4, -275.83) * mm});
            skLineSegment(sketch, "E220", {"start": v(-15.78, -288.15) * mm, "end": v(9.62, -294.5) * mm});
            skLineSegment(sketch, "E221", {"start": v(25.4, -282.18) * mm, "end": v(25.4, 0) * mm});
            skArc(sketch, "E222.filletArc", {"start": v(-25.4, -275.83) * mm, "mid": v(-22.71, -283.65) * mm, "end": v(-15.78, -288.15) * mm});
            skArc(sketch, "E223.filletArc", {"start": v(9.62, -294.5) * mm, "mid": v(20.52, -292.2) * mm, "end": v(25.4, -282.18) * mm});
            skPoint(sketch, "E224.MirrorP", {"position": v(-1763.83, 631.7) * mm});
            skPoint(sketch, "E225", {"position": v(-25.4, 323.85) * mm});
            skPoint(sketch, "E226", {"position": v(25.4, 311.15) * mm});
            skLineSegment(sketch, "E227", {"start": v(-25.4, 0) * mm, "end": v(-25.4, 307.58) * mm});
            skLineSegment(sketch, "E228", {"start": v(-9.62, 319.9) * mm, "end": v(15.78, 313.55) * mm});
            skLineSegment(sketch, "E229", {"start": v(25.4, 301.23) * mm, "end": v(25.4, 0) * mm});
            skArc(sketch, "E230.filletArc", {"start": v(-9.62, 319.9) * mm, "mid": v(-20.52, 317.6) * mm, "end": v(-25.4, 307.58) * mm});
            skArc(sketch, "E231.filletArc", {"start": v(25.4, 301.23) * mm, "mid": v(22.71, 309.05) * mm, "end": v(15.78, 313.55) * mm});
            skSolve(sketch);
        }
        {
            var Q0;
            Q0=qSketchRegion(id+"F24",true);
            extrude(context, id + "F25", {"entities" : qUnion([Q0]), "depth" : 6.35 * mm});
        }
        {
            var Q0;
            Q0=makeQuery(id+"F25.opExtrude","CAP_FACE",FACE,{"disambiguationData":[OSD([sQuery(id+"F24.wireOp",EDGE,"E219"),sQuery(id+"F24.wireOp",EDGE,"E220"),sQuery(id+"F24.wireOp",EDGE,"E221"),sQuery(id+"F24.wireOp",EDGE,"E222.filletArc"),sQuery(id+"F24.wireOp",EDGE,"E223.filletArc"),sQuery(id+"F24.wireOp",EDGE,"E227"),sQuery(id+"F24.wireOp",EDGE,"E228"),sQuery(id+"F24.wireOp",EDGE,"E229"),sQuery(id+"F24.wireOp",EDGE,"E230.filletArc"),sQuery(id+"F24.wireOp",EDGE,"E231.filletArc")])],"isStart":false});
            var sketch = newSketch(context, id + "F26", { "sketchPlane" : qUnion([Q0])});
            skPoint(sketch, "E232", {"position": v(0, 0) * mm});
            skPoint(sketch, "E233", {"position": v(-28.58, 0) * mm});
            skPoint(sketch, "E234", {"position": v(-28.57, -284.16) * mm});
            skPoint(sketch, "E235", {"position": v(28.58, 0) * mm});
            skPoint(sketch, "E236", {"position": v(28.58, -300.04) * mm});
            skLineSegment(sketch, "E237", {"start": v(-28.58, 0) * mm, "end": v(-28.57, -274.5) * mm});
            skLineSegment(sketch, "E238", {"start": v(-19.27, -286.75) * mm, "end": v(12.48, -295.57) * mm});
            skLineSegment(sketch, "E239", {"start": v(28.58, -283.33) * mm, "end": v(28.58, 0) * mm});
            skArc(sketch, "E240.filletArc", {"start": v(-28.57, -274.5) * mm, "mid": v(-25.99, -282.2) * mm, "end": v(-19.27, -286.75) * mm});
            skArc(sketch, "E241.filletArc", {"start": v(12.48, -295.57) * mm, "mid": v(23.56, -293.44) * mm, "end": v(28.57, -283.33) * mm});
            skPoint(sketch, "E242.MirrorP", {"position": v(-2122.86, 677.9) * mm});
            skPoint(sketch, "E243", {"position": v(-28.58, 325.44) * mm});
            skPoint(sketch, "E244", {"position": v(28.57, 309.56) * mm});
            skLineSegment(sketch, "E245", {"start": v(-28.58, 0) * mm, "end": v(-28.58, 308.73) * mm});
            skLineSegment(sketch, "E246", {"start": v(-12.48, 320.97) * mm, "end": v(19.27, 312.15) * mm});
            skLineSegment(sketch, "E247", {"start": v(28.57, 299.9) * mm, "end": v(28.58, 0) * mm});
            skArc(sketch, "E248.filletArc", {"start": v(-12.48, 320.97) * mm, "mid": v(-23.56, 318.84) * mm, "end": v(-28.58, 308.73) * mm});
            skArc(sketch, "E249.filletArc", {"start": v(28.57, 299.9) * mm, "mid": v(25.99, 307.6) * mm, "end": v(19.27, 312.15) * mm});
            skSolve(sketch);
        }
        {
            var Q0;
            Q0=qSketchRegion(id+"F26",true);
            extrude(context, id + "F27", {"entities" : qUnion([Q0]), "depth" : 6.35 * mm});
        }
        {
            var Q0;
            Q0=makeQuery(id+"F27.opExtrude","CAP_FACE",FACE,{"disambiguationData":[OSD([sQuery(id+"F26.wireOp",EDGE,"E237"),sQuery(id+"F26.wireOp",EDGE,"E238"),sQuery(id+"F26.wireOp",EDGE,"E239"),sQuery(id+"F26.wireOp",EDGE,"E240.filletArc"),sQuery(id+"F26.wireOp",EDGE,"E241.filletArc"),sQuery(id+"F26.wireOp",EDGE,"E245"),sQuery(id+"F26.wireOp",EDGE,"E246"),sQuery(id+"F26.wireOp",EDGE,"E247"),sQuery(id+"F26.wireOp",EDGE,"E248.filletArc"),sQuery(id+"F26.wireOp",EDGE,"E249.filletArc")])],"isStart":false});
            var sketch = newSketch(context, id + "F28", { "sketchPlane" : qUnion([Q0])});
            skPoint(sketch, "E250", {"position": v(0, 0) * mm});
            skPoint(sketch, "E251", {"position": v(-31.75, 0) * mm});
            skPoint(sketch, "E252", {"position": v(-31.75, -282.58) * mm});
            skPoint(sketch, "E253", {"position": v(31.75, 0) * mm});
            skPoint(sketch, "E254", {"position": v(31.75, -301.63) * mm});
            skLineSegment(sketch, "E255", {"start": v(-31.75, 0) * mm, "end": v(-31.75, -273.13) * mm});
            skLineSegment(sketch, "E256", {"start": v(-22.7, -285.3) * mm, "end": v(15.4, -296.72) * mm});
            skLineSegment(sketch, "E257", {"start": v(31.75, -284.56) * mm, "end": v(31.75, 0) * mm});
            skArc(sketch, "E258.filletArc", {"start": v(-31.75, -273.13) * mm, "mid": v(-29.24, -280.7) * mm, "end": v(-22.7, -285.3) * mm});
            skArc(sketch, "E259.filletArc", {"start": v(15.4, -296.72) * mm, "mid": v(26.63, -294.74) * mm, "end": v(31.75, -284.56) * mm});
            skPoint(sketch, "E260.MirrorP", {"position": v(-2131.05, 728.59) * mm});
            skPoint(sketch, "E261", {"position": v(-31.75, 327.03) * mm});
            skPoint(sketch, "E262", {"position": v(31.75, 307.98) * mm});
            skLineSegment(sketch, "E263", {"start": v(-31.75, 0) * mm, "end": v(-31.75, 309.96) * mm});
            skLineSegment(sketch, "E264", {"start": v(-15.4, 322.12) * mm, "end": v(22.7, 310.7) * mm});
            skLineSegment(sketch, "E265", {"start": v(31.75, 298.53) * mm, "end": v(31.75, 0) * mm});
            skArc(sketch, "E266.filletArc", {"start": v(-15.4, 322.12) * mm, "mid": v(-26.63, 320.14) * mm, "end": v(-31.75, 309.96) * mm});
            skArc(sketch, "E267.filletArc", {"start": v(31.75, 298.53) * mm, "mid": v(29.24, 306.1) * mm, "end": v(22.7, 310.7) * mm});
            skSolve(sketch);
        }
        {
            var Q0;
            Q0=qSketchRegion(id+"F28",true);
            extrude(context, id + "F29", {"entities" : qUnion([Q0]), "depth" : 6.35 * mm});
        }
        {
            var Q0;
            {var subQ12=makeQuery(id+"F27.opExtrude","CAP_EDGE",EDGE,{"disambiguationData":[OSD([sQuery(id+"F26.wireOp",EDGE,"E241.filletArc")])],"isStart":false});Q0=makeQuery(id+"F28.imprint","IMPRINT",FACE,{"disambiguationData":[TD([[makeQuery(id+"F28.imprint","IMPRINT",EDGE,{"derivedFrom":subQ12}),1.0]])]});}
            var sketch = newSketch(context, id + "F30", { "sketchPlane" : qUnion([Q0])});
            skPoint(sketch, "E268", {"position": v(0, 0) * mm});
            skPoint(sketch, "E269", {"position": v(-34.93, 0) * mm});
            skPoint(sketch, "E270", {"position": v(-34.93, -280.99) * mm});
            skPoint(sketch, "E271", {"position": v(34.93, 0) * mm});
            skPoint(sketch, "E272", {"position": v(34.93, -303.21) * mm});
            skLineSegment(sketch, "E273", {"start": v(-34.93, 0) * mm, "end": v(-34.93, -271.7) * mm});
            skLineSegment(sketch, "E274", {"start": v(-26.08, -283.8) * mm, "end": v(18.37, -297.95) * mm});
            skLineSegment(sketch, "E275", {"start": v(34.93, -285.84) * mm, "end": v(34.93, 0) * mm});
            skArc(sketch, "E276.filletArc", {"start": v(-34.93, -271.7) * mm, "mid": v(-32.48, -279.2) * mm, "end": v(-26.08, -283.8) * mm});
            skArc(sketch, "E277.filletArc", {"start": v(18.37, -297.95) * mm, "mid": v(29.72, -296.1) * mm, "end": v(34.92, -285.84) * mm});
            skPoint(sketch, "E278.MirrorP", {"position": v(-2087.8, 736.08) * mm});
            skPoint(sketch, "E279", {"position": v(-34.93, 328.61) * mm});
            skPoint(sketch, "E280", {"position": v(34.92, 306.39) * mm});
            skLineSegment(sketch, "E281", {"start": v(-34.93, 0) * mm, "end": v(-34.93, 311.24) * mm});
            skLineSegment(sketch, "E282", {"start": v(-18.37, 323.35) * mm, "end": v(26.08, 309.2) * mm});
            skLineSegment(sketch, "E283", {"start": v(34.92, 297.1) * mm, "end": v(34.93, 0) * mm});
            skArc(sketch, "E284.filletArc", {"start": v(-18.37, 323.35) * mm, "mid": v(-29.72, 321.5) * mm, "end": v(-34.93, 311.24) * mm});
            skArc(sketch, "E285.filletArc", {"start": v(34.92, 297.1) * mm, "mid": v(32.48, 304.6) * mm, "end": v(26.08, 309.2) * mm});
            skSolve(sketch);
        }
        {
            var Q0;
            Q0=qSketchRegion(id+"F30",true);
            extrude(context, id + "F31", {"entities" : qUnion([Q0]), "depth" : 6.35 * mm});
        }
        {
            var Q0;
            Q0=makeQuery(id+"F31.opExtrude","CAP_FACE",FACE,{"disambiguationData":[OSD([sQuery(id+"F30.wireOp",EDGE,"E273"),sQuery(id+"F30.wireOp",EDGE,"E274"),sQuery(id+"F30.wireOp",EDGE,"E275"),sQuery(id+"F30.wireOp",EDGE,"E276.filletArc"),sQuery(id+"F30.wireOp",EDGE,"E277.filletArc"),sQuery(id+"F30.wireOp",EDGE,"E281"),sQuery(id+"F30.wireOp",EDGE,"E282"),sQuery(id+"F30.wireOp",EDGE,"E283"),sQuery(id+"F30.wireOp",EDGE,"E284.filletArc"),sQuery(id+"F30.wireOp",EDGE,"E285.filletArc")])],"isStart":false});
            var sketch = newSketch(context, id + "F32", { "sketchPlane" : qUnion([Q0])});
            skPoint(sketch, "E286", {"position": v(0, 0) * mm});
            skPoint(sketch, "E287", {"position": v(-38.1, 0) * mm});
            skPoint(sketch, "E288", {"position": v(-38.1, -279.4) * mm});
            skPoint(sketch, "E289", {"position": v(38.1, 0) * mm});
            skPoint(sketch, "E290", {"position": v(38.1, -304.8) * mm});
            skLineSegment(sketch, "E291", {"start": v(-38.1, 0) * mm, "end": v(-38.1, -270.25) * mm});
            skLineSegment(sketch, "E292", {"start": v(-29.42, -282.3) * mm, "end": v(21.38, -299.23) * mm});
            skLineSegment(sketch, "E293", {"start": v(38.1, -287.18) * mm, "end": v(38.1, 0) * mm});
            skArc(sketch, "E294.filletArc", {"start": v(-38.1, -270.25) * mm, "mid": v(-35.7, -277.67) * mm, "end": v(-29.42, -282.3) * mm});
            skArc(sketch, "E295.filletArc", {"start": v(21.38, -299.23) * mm, "mid": v(32.83, -297.48) * mm, "end": v(38.1, -287.18) * mm});
            skPoint(sketch, "E296.MirrorP", {"position": v(-2058.68, 783.5) * mm});
            skPoint(sketch, "E297", {"position": v(-38.1, 330.2) * mm});
            skPoint(sketch, "E298", {"position": v(38.1, 304.8) * mm});
            skLineSegment(sketch, "E299", {"start": v(-38.1, 0) * mm, "end": v(-38.1, 312.58) * mm});
            skLineSegment(sketch, "E300", {"start": v(-21.38, 324.63) * mm, "end": v(29.42, 307.7) * mm});
            skLineSegment(sketch, "E301", {"start": v(38.1, 295.65) * mm, "end": v(38.1, 0) * mm});
            skArc(sketch, "E302.filletArc", {"start": v(-21.38, 324.63) * mm, "mid": v(-32.83, 322.88) * mm, "end": v(-38.1, 312.58) * mm});
            skArc(sketch, "E303.filletArc", {"start": v(38.1, 295.65) * mm, "mid": v(35.7, 303.07) * mm, "end": v(29.42, 307.7) * mm});
            skSolve(sketch);
        }
        {
            var Q0;
            Q0=qSketchRegion(id+"F32",true);
            extrude(context, id + "F33", {"entities" : qUnion([Q0]), "depth" : 6.35 * mm});
        }
        {
            var Q0;
            Q0=qCreatedBy(makeId("Top.planeOp"),FACE);
            var sketch = newSketch(context, id + "F34", { "sketchPlane" : qUnion([Q0])});
            skLineSegment(sketch, "E304", {"start": v(0, 0) * mm, "end": v(0, -271) * mm, "construction": true});
            skCircle(sketch, "E305", {"center": v(0, -257.95) * mm, "radius": 8.8 * mm});
            skCircle(sketch, "E306.0.1.0", {"center": v(0, -196.99) * mm, "radius": 8.8 * mm});
            skCircle(sketch, "E306.0.2.0", {"center": v(0, -136.03) * mm, "radius": 8.8 * mm});
            skCircle(sketch, "E306.0.3.0", {"center": v(0, -75.07) * mm, "radius": 8.8 * mm});
            skCircle(sketch, "E306.0.4.0", {"center": v(0, -14.1) * mm, "radius": 8.8 * mm});
            skLineSegment(sketch, "E306.direction1", {"start": v(0, -257.95) * mm, "end": v(25.4, -257.95) * mm, "construction": true});
            skLineSegment(sketch, "E306.direction2", {"start": v(0, -257.95) * mm, "end": v(0, -196.99) * mm, "construction": true});
            skLineSegment(sketch, "E307.MirrorCS", {"start": v(0, 257.95) * mm, "end": v(0, 196.99) * mm, "construction": true});
            skLineSegment(sketch, "E308.MirrorCS", {"start": v(0, 0) * mm, "end": v(0, 271) * mm, "construction": true});
            skLineSegment(sketch, "E309.MirrorCS", {"start": v(0, 257.95) * mm, "end": v(25.4, 257.95) * mm, "construction": true});
            skCircle(sketch, "E310.MirrorC", {"center": v(0, 14.1) * mm, "radius": 8.8 * mm});
            skCircle(sketch, "E311.MirrorC", {"center": v(0, 136.03) * mm, "radius": 8.8 * mm});
            skCircle(sketch, "E312.MirrorC", {"center": v(0, 75.07) * mm, "radius": 8.8 * mm});
            skCircle(sketch, "E313.MirrorC", {"center": v(0, 257.95) * mm, "radius": 8.8 * mm});
            skCircle(sketch, "E314.MirrorC", {"center": v(0, 196.99) * mm, "radius": 8.8 * mm});
            skSolve(sketch);
        }
        {
            var Q0;
            Q0 = qSketchRegion(id + "F34", true);
            extrude(context, id + "F35", {"entities" : qUnion([Q0]), "operationType" : NewBodyOperationType.ADD, "endBound" : BoundingType.SYMMETRIC, "depth" : 25.4 * mm, "hasDraft" : true, "draftAngle" : 20 * degree});
        }
    });
